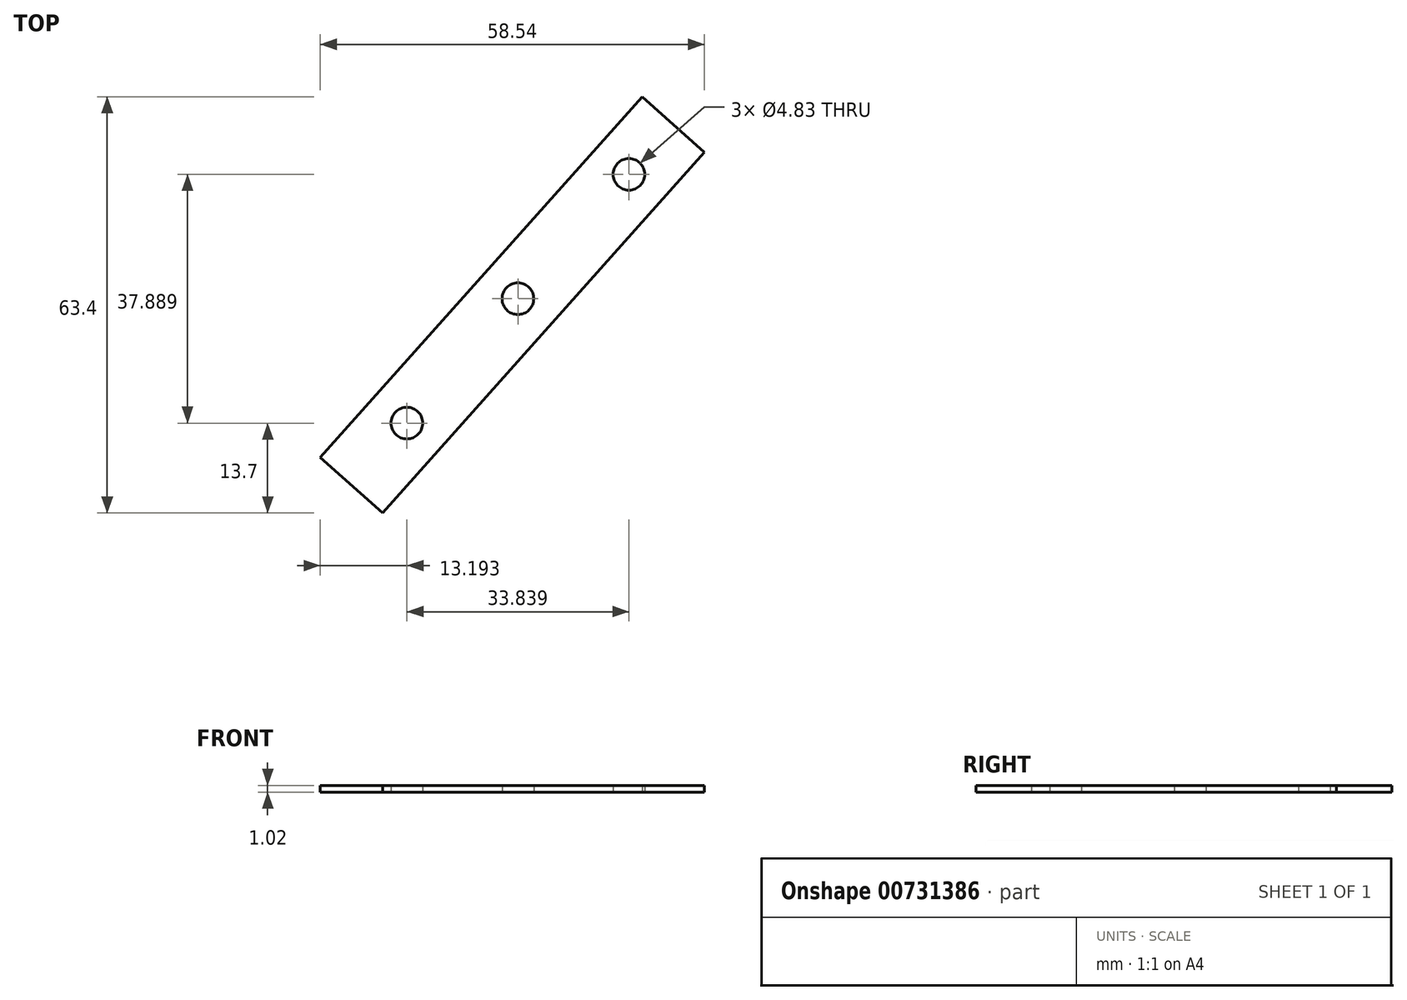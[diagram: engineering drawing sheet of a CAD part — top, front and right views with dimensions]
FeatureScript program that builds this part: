
annotation { "Feature Type Name" : "Feature", "Feature Type Description" : "" }
export const myFeature = defineFeature(function(context is Context, id is Id, definition is map)
    precondition{}
    {
        {
            var Q0;
            Q0=qCreatedBy(makeId("Top.planeOp"),FACE);
            var sketch = newSketch(context, id + "F0", { "sketchPlane" : qUnion([Q0])});
            skArc(sketch, "E0", {"start": v(-16.8, 0) * mm, "mid": v(15.33, 6.86) * mm, "end": v(-11.18, -12.52) * mm});
            skArc(sketch, "E1", {"start": v(-90.45, 0) * mm, "mid": v(82.56, 36.96) * mm, "end": v(-60.25, -67.46) * mm});
            skLineSegment(sketch, "E2", {"start": v(-90.45, 0) * mm, "end": v(-16.8, 0) * mm});
            skLineSegment(sketch, "E3", {"start": v(-11.18, -12.52) * mm, "end": v(-60.25, -67.46) * mm});
            skLineSegment(sketch, "E4", {"start": v(-69.72, -59) * mm, "end": v(-20.66, -4.06) * mm});
            skLineSegment(sketch, "E5", {"start": v(-20.66, -4.06) * mm, "end": v(-11.18, -12.52) * mm});
            skLineSegment(sketch, "E6", {"start": v(-69.72, -59) * mm, "end": v(-60.25, -67.46) * mm});
            skSolve(sketch);
        }
        {
            var Q0;
            Q0=makeQuery(id+"F0.imprint","IMPRINT",FACE,{"disambiguationData":[TD([[makeQuery(id+"F0.imprint","IMPRINT",EDGE,{"derivedFrom":sQuery(id+"F0.wireOp",EDGE,"E0")}),1.0]])]});
            var Q1;
            Q1=makeQuery(id+"F0.imprint","IMPRINT",FACE,{"disambiguationData":[TD([[makeQuery(id+"F0.imprint","IMPRINT",EDGE,{"derivedFrom":sQuery(id+"F0.wireOp",EDGE,"E3")}),-1.0]])]});
            extrude(context, id + "F1", {"entities" : qUnion([Q0, Q1]), "depth" : 1.02 * mm, "offsetDistance" : 25.4 * mm});
        }
        {
            var Q0;
            Q0=qCreatedBy(makeId("Top.planeOp"),FACE);
            var sketch = newSketch(context, id + "F2", { "sketchPlane" : qUnion([Q0])});
            skPoint(sketch, "E7", {"position": v(-77.75, 6.35) * mm});
            skPoint(sketch, "E8", {"position": v(-52.35, 6.35) * mm});
            skPoint(sketch, "E9", {"position": v(-26.95, 6.35) * mm});
            skPoint(sketch, "E10", {"position": v(-56.53, -53.76) * mm});
            skPoint(sketch, "E11", {"position": v(-39.6, -34.82) * mm});
            skPoint(sketch, "E12", {"position": v(-22.69, -15.87) * mm});
            skLineSegment(sketch, "E13", {"start": v(-56.53, -53.76) * mm, "end": v(-22.69, -15.87) * mm, "construction": true});
            skLineSegment(sketch, "E14", {"start": v(-77.75, 6.35) * mm, "end": v(-26.95, 6.35) * mm, "construction": true});
            skSolve(sketch);
        }
        {
            var Q0;
            Q0=sQuery(id+"F2.wireOp",VERTEX,"E14.start");
            var Q1;
            Q1=sQuery(id+"F2.wireOp",VERTEX,"E8");
            var Q2;
            Q2=sQuery(id+"F2.wireOp",VERTEX,"E9");
            var Q3;
            Q3=sQuery(id+"F2.wireOp",VERTEX,"E12");
            var Q4;
            Q4=sQuery(id+"F2.wireOp",VERTEX,"E11");
            var Q5;
            Q5=sQuery(id+"F2.wireOp",VERTEX,"E10");
            var Q6;
            Q6=makeQuery(id+"F1.opExtrude","SWEPT_BODY",BODY,{"disambiguationData":[OSD([sQuery(id+"F0.wireOp",EDGE,"E0"),sQuery(id+"F0.wireOp",EDGE,"E1"),sQuery(id+"F0.wireOp",EDGE,"E2"),sQuery(id+"F0.wireOp",EDGE,"E4"),sQuery(id+"F0.wireOp",EDGE,"E5"),sQuery(id+"F0.wireOp",EDGE,"E6")])]});
            hole(context, id + "F3", {"style" : HoleStyle.SIMPLE, "endStyle" : HoleEndStyle.THROUGH, "oppositeDirection" : true, "holeDiameter" : 4.83 * mm, "majorDiameter" : 6.35 * mm, "isTappedThrough" : true, "tappedDepth" : 12.7 * mm, "tapClearance" : 3, "locations" : qUnion([Q0, Q1, Q2, Q3, Q4, Q5]), "scope" : qUnion([Q6])});
        }
    });
